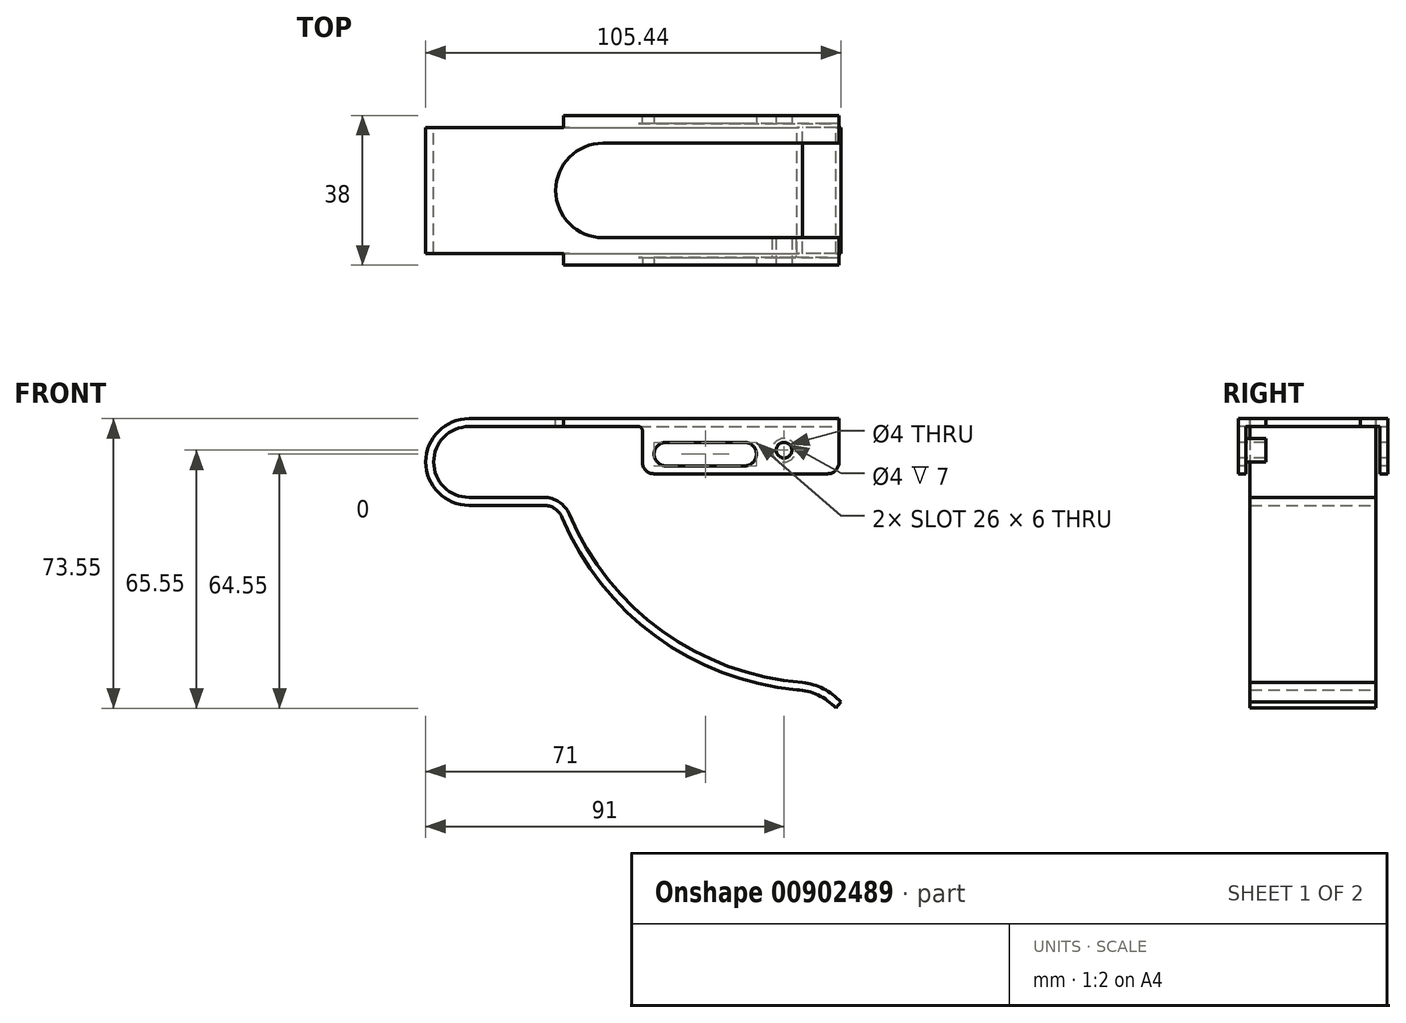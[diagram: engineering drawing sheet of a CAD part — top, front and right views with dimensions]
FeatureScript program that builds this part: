
annotation { "Feature Type Name" : "Feature", "Feature Type Description" : "" }
export const myFeature = defineFeature(function(context is Context, id is Id, definition is map)
    precondition{}
    {
        {
            var Q0;
            Q0=qCreatedBy(makeId("Front.planeOp"),FACE);
            var sketch = newSketch(context, id + "F0", { "sketchPlane" : qUnion([Q0])});
            skArc(sketch, "E0", {"start": v(0, 11) * mm, "mid": v(-11, 0) * mm, "end": v(0, -11) * mm});
            skLineSegment(sketch, "E1", {"start": v(0, 11) * mm, "end": v(94, 11) * mm});
            skLineSegment(sketch, "E2", {"start": v(0, -11) * mm, "end": v(19, -11) * mm});
            skArc(sketch, "E3", {"start": v(23.61, -14.06) * mm, "mid": v(47.38, -44.23) * mm, "end": v(83.28, -57.89) * mm});
            skArc(sketch, "E4", {"start": v(93.14, -62.55) * mm, "mid": v(88.68, -59.22) * mm, "end": v(83.28, -57.89) * mm});
            skPoint(sketch, "E5.visualSharp", {"position": v(22.4, -11) * mm});
            skArc(sketch, "E5.filletArc", {"start": v(23.61, -14.06) * mm, "mid": v(21.77, -11.84) * mm, "end": v(19, -11) * mm});
            skLineSegment(sketch, "E6.0", {"start": v(0, 9) * mm, "end": v(94, 9) * mm});
            skArc(sketch, "E7.0", {"start": v(0, 9) * mm, "mid": v(-9, 0) * mm, "end": v(0, -9) * mm});
            skLineSegment(sketch, "E8.0", {"start": v(0, -9) * mm, "end": v(19, -9) * mm});
            skArc(sketch, "E9.0", {"start": v(25.9, -14.87) * mm, "mid": v(23.53, -10.67) * mm, "end": v(19, -9) * mm});
            skArc(sketch, "E10.0", {"start": v(25.45, -13.3) * mm, "mid": v(49.07, -42.99) * mm, "end": v(84.7, -56) * mm});
            skArc(sketch, "E11.0", {"start": v(94.44, -61) * mm, "mid": v(90.01, -57.64) * mm, "end": v(84.7, -56) * mm});
            skLineSegment(sketch, "E12", {"start": v(93.14, -62.55) * mm, "end": v(94.44, -61) * mm});
            skLineSegment(sketch, "E13", {"start": v(94, 11) * mm, "end": v(94, 9) * mm});
            skLineSegment(sketch, "E14", {"start": v(94.44, -61) * mm, "end": v(131.24, -61) * mm, "construction": true});
            skSolve(sketch);
        }
        {
            var Q0;
            Q0 = qSketchRegion(id + "F0", true);
            extrude(context, id + "F1", {"entities" : qUnion([Q0]), "depth" : 16 * mm, "offsetDistance" : 25 * mm});
        }
        {
            var Q0;
            Q0=makeQuery(id+"F1.opExtrude","SWEPT_FACE",FACE,{"disambiguationData":[OSD([sQuery(id+"F0.wireOp",EDGE,"E1")])]});
            var sketch = newSketch(context, id + "F2", { "sketchPlane" : qUnion([Q0])});
            skLineSegment(sketch, "E15.bottom", {"start": v(94, -16) * mm, "end": v(24, -16) * mm});
            skLineSegment(sketch, "E15.top", {"start": v(94, -19) * mm, "end": v(24, -19) * mm});
            skLineSegment(sketch, "E15.left", {"start": v(94, -16) * mm, "end": v(94, -19) * mm});
            skLineSegment(sketch, "E15.right", {"start": v(24, -16) * mm, "end": v(24, -19) * mm});
            skSolve(sketch);
        }
        {
            var Q0;
            Q0=makeQuery(id+"F2.imprint","IMPRINT",FACE,{"disambiguationData":[TD([[makeQuery(id+"F2.imprint","IMPRINT",EDGE,{"derivedFrom":sQuery(id+"F2.wireOp",EDGE,"E15.bottom")}),-1.0]])]});
            extrude(context, id + "F3", {"entities" : qUnion([Q0]), "operationType" : NewBodyOperationType.ADD, "oppositeDirection" : true, "depth" : 2 * mm, "offsetDistance" : 25 * mm});
        }
        {
            var Q0;
            Q0=makeQuery(id+"F3.opExtrude","SWEPT_FACE",FACE,{"disambiguationData":[OSD([sQuery(id+"F2.wireOp",EDGE,"E15.top")])]});
            var sketch = newSketch(context, id + "F4", { "sketchPlane" : qUnion([Q0])});
            skLineSegment(sketch, "E16.bottom", {"start": v(94, 11) * mm, "end": v(44, 11) * mm});
            skLineSegment(sketch, "E16.top", {"start": v(94, -3) * mm, "end": v(44, -3) * mm});
            skLineSegment(sketch, "E16.left", {"start": v(94, 11) * mm, "end": v(94, -3) * mm});
            skLineSegment(sketch, "E16.right", {"start": v(44, 11) * mm, "end": v(44, -3) * mm});
            skSolve(sketch);
        }
        {
            var Q0;
            Q0 = qSketchRegion(id + "F4", true);
            extrude(context, id + "F5", {"entities" : qUnion([Q0]), "operationType" : NewBodyOperationType.ADD, "oppositeDirection" : true, "depth" : 2 * mm, "offsetDistance" : 25 * mm});
        }
        {
            var Q0;
            Q0=makeQuery(id+"F5.boolean.opBoolean","INTERSECT",EDGE,{"derivedFrom":[makeQuery(id+"F3.boolean.opBoolean","MERGE",FACE,{"derivedFrom":[makeQuery(id+"F1.opExtrude","SWEPT_FACE",FACE,{"disambiguationData":[OSD([sQuery(id+"F0.wireOp",EDGE,"E6.0")])]}),makeQuery(id+"F3.opExtrude","CAP_FACE",FACE,{"disambiguationData":[OSD([sQuery(id+"F2.wireOp",EDGE,"E15.bottom"),sQuery(id+"F2.wireOp",EDGE,"E15.top"),sQuery(id+"F2.wireOp",EDGE,"E15.left"),sQuery(id+"F2.wireOp",EDGE,"E15.right")])],"isStart":false})]}),makeQuery(id+"F5.opExtrude","SWEPT_FACE",FACE,{"disambiguationData":[OSD([sQuery(id+"F4.wireOp",EDGE,"E16.right")])]})]});
            fillet(context, id + "F6", {"entities" : qUnion([Q0]), "radius" : 1 * mm, "tangentPropagation" : true, "allowEdgeOverflow" : false});
        }
        {
            var Q0;
            Q0=makeQuery(id+"F1.opExtrude","SWEPT_BODY",BODY,{"disambiguationData":[OSD([sQuery(id+"F0.wireOp",EDGE,"E0"),sQuery(id+"F0.wireOp",EDGE,"E1"),sQuery(id+"F0.wireOp",EDGE,"E2"),sQuery(id+"F0.wireOp",EDGE,"E3"),sQuery(id+"F0.wireOp",EDGE,"E4"),sQuery(id+"F0.wireOp",EDGE,"E5.filletArc"),sQuery(id+"F0.wireOp",EDGE,"E6.0"),sQuery(id+"F0.wireOp",EDGE,"E7.0"),sQuery(id+"F0.wireOp",EDGE,"E8.0"),sQuery(id+"F0.wireOp",EDGE,"E9.0"),sQuery(id+"F0.wireOp",EDGE,"E10.0"),sQuery(id+"F0.wireOp",EDGE,"E11.0"),sQuery(id+"F0.wireOp",EDGE,"E12"),sQuery(id+"F0.wireOp",EDGE,"E13")])]});
            var Q1;
            Q1=qCreatedBy(makeId("Front.planeOp"),FACE);
            mirror(context, id + "F7", {"operationType" : NewBodyOperationType.ADD, "entities" : qUnion([Q0]), "mirrorPlane" : qUnion([Q1])});
        }
        {
            var Q0;
            {var subQ0=makeQuery(id+"F3.boolean.opBoolean","MERGE",FACE,{"derivedFrom":[makeQuery(id+"F1.opExtrude","SWEPT_FACE",FACE,{"disambiguationData":[OSD([sQuery(id+"F0.wireOp",EDGE,"E1")])]}),makeQuery(id+"F3.opExtrude","CAP_FACE",FACE,{"disambiguationData":[OSD([sQuery(id+"F2.wireOp",EDGE,"E15.bottom"),sQuery(id+"F2.wireOp",EDGE,"E15.top"),sQuery(id+"F2.wireOp",EDGE,"E15.left"),sQuery(id+"F2.wireOp",EDGE,"E15.right")])],"isStart":true})]});Q0=makeQuery(id+"F7.boolean.opBoolean","MERGE",FACE,{"derivedFrom":[subQ0,makeQuery(id+"F7.opPattern","COPY",FACE,{"derivedFrom":subQ0,"instanceName":"1"})]});}
            var sketch = newSketch(context, id + "F8", { "sketchPlane" : qUnion([Q0])});
            skArc(sketch, "E17", {"start": v(34, 12) * mm, "mid": v(22, 0) * mm, "end": v(34, -12) * mm});
            skLineSegment(sketch, "E18", {"start": v(34, 12) * mm, "end": v(94, 12) * mm});
            skLineSegment(sketch, "E19", {"start": v(34, -12) * mm, "end": v(94, -12) * mm});
            skLineSegment(sketch, "E20", {"start": v(94, 12) * mm, "end": v(94, -12) * mm});
            skSolve(sketch);
        }
        {
            var Q0;
            Q0 = qSketchRegion(id + "F8", true);
            extrude(context, id + "F9", {"entities" : qUnion([Q0]), "operationType" : NewBodyOperationType.REMOVE, "oppositeDirection" : true, "depth" : 2 * mm, "offsetDistance" : 25 * mm});
        }
        {
            var Q0;
            Q0=makeQuery(id+"F5.boolean.opBoolean","MERGE",FACE,{"derivedFrom":[makeQuery(id+"F3.opExtrude","SWEPT_FACE",FACE,{"disambiguationData":[OSD([sQuery(id+"F2.wireOp",EDGE,"E15.top")])]}),makeQuery(id+"F5.opExtrude","CAP_FACE",FACE,{"disambiguationData":[OSD([sQuery(id+"F4.wireOp",EDGE,"E16.bottom"),sQuery(id+"F4.wireOp",EDGE,"E16.top"),sQuery(id+"F4.wireOp",EDGE,"E16.left"),sQuery(id+"F4.wireOp",EDGE,"E16.right")])],"isStart":true})]});
            var sketch = newSketch(context, id + "F10", { "sketchPlane" : qUnion([Q0])});
            skLineSegment(sketch, "E21", {"start": v(50, 2) * mm, "end": v(70, 2) * mm});
            skArc(sketch, "E22.0.startCap", {"start": v(50, -1) * mm, "mid": v(47, 2) * mm, "end": v(50, 5) * mm});
            skArc(sketch, "E22.0.endCap", {"start": v(70, 5) * mm, "mid": v(73, 2) * mm, "end": v(70, -1) * mm});
            skLineSegment(sketch, "E22.0.left", {"start": v(50, 5) * mm, "end": v(70, 5) * mm});
            skLineSegment(sketch, "E22.0.right", {"start": v(50, -1) * mm, "end": v(70, -1) * mm});
            skSolve(sketch);
        }
        {
            var Q0;
            Q0 = qSketchRegion(id + "F10", true);
            extrude(context, id + "F11", {"entities" : qUnion([Q0]), "operationType" : NewBodyOperationType.REMOVE, "endBound" : BoundingType.THROUGH_ALL, "oppositeDirection" : true, "depth" : 25 * mm, "offsetDistance" : 25 * mm});
        }
        {
            var Q0;
            Q0=makeQuery(id+"F5.boolean.opBoolean","MERGE",FACE,{"derivedFrom":[makeQuery(id+"F3.opExtrude","SWEPT_FACE",FACE,{"disambiguationData":[OSD([sQuery(id+"F2.wireOp",EDGE,"E15.top")])]}),makeQuery(id+"F5.opExtrude","CAP_FACE",FACE,{"disambiguationData":[OSD([sQuery(id+"F4.wireOp",EDGE,"E16.bottom"),sQuery(id+"F4.wireOp",EDGE,"E16.top"),sQuery(id+"F4.wireOp",EDGE,"E16.left"),sQuery(id+"F4.wireOp",EDGE,"E16.right")])],"isStart":true})]});
            var sketch = newSketch(context, id + "F12", { "sketchPlane" : qUnion([Q0])});
            skPoint(sketch, "E23", {"position": v(80, 3) * mm});
            skSolve(sketch);
        }
        {
            var Q0;
            Q0=sQuery(id+"F12.wireOp",VERTEX,"E23");
            var Q1;
            Q1=makeQuery(id+"F1.opExtrude","SWEPT_BODY",BODY,{"disambiguationData":[OSD([sQuery(id+"F0.wireOp",EDGE,"E0"),sQuery(id+"F0.wireOp",EDGE,"E1"),sQuery(id+"F0.wireOp",EDGE,"E2"),sQuery(id+"F0.wireOp",EDGE,"E3"),sQuery(id+"F0.wireOp",EDGE,"E4"),sQuery(id+"F0.wireOp",EDGE,"E5.filletArc"),sQuery(id+"F0.wireOp",EDGE,"E6.0"),sQuery(id+"F0.wireOp",EDGE,"E7.0"),sQuery(id+"F0.wireOp",EDGE,"E8.0"),sQuery(id+"F0.wireOp",EDGE,"E9.0"),sQuery(id+"F0.wireOp",EDGE,"E10.0"),sQuery(id+"F0.wireOp",EDGE,"E11.0"),sQuery(id+"F0.wireOp",EDGE,"E12"),sQuery(id+"F0.wireOp",EDGE,"E13")])]});
            hole(context, id + "F13", {"style" : HoleStyle.SIMPLE, "endStyle" : HoleEndStyle.THROUGH, "holeDiameter" : 4 * mm, "majorDiameter" : 5 * mm, "isTappedThrough" : true, "tappedDepth" : 12 * mm, "tapClearance" : 3, "locations" : qUnion([Q0]), "scope" : qUnion([Q1])});
        }
        {
            var Q0;
            Q0=makeQuery(id+"F5.opExtrude","CAP_FACE",FACE,{"disambiguationData":[OSD([sQuery(id+"F4.wireOp",EDGE,"E16.bottom"),sQuery(id+"F4.wireOp",EDGE,"E16.top"),sQuery(id+"F4.wireOp",EDGE,"E16.left"),sQuery(id+"F4.wireOp",EDGE,"E16.right")])],"isStart":false});
            var sketch = newSketch(context, id + "F14", { "sketchPlane" : qUnion([Q0])});
            skCircle(sketch, "E24.0", {"center": v(-80, 3) * mm, "radius": 2 * mm});
            skCircle(sketch, "E25.0", {"center": v(-80, 3) * mm, "radius": 3 * mm});
            skSolve(sketch);
        }
        {
            var Q0;
            Q0 = qSketchRegion(id + "F14", true);
            extrude(context, id + "F15", {"entities" : qUnion([Q0]), "operationType" : NewBodyOperationType.ADD, "depth" : 5 * mm, "offsetDistance" : 25 * mm});
        }
        {
            var Q0;
            Q0=makeQuery(id+"F5.opExtrude","SWEPT_EDGE",EDGE,{"disambiguationData":[OSD([sQuery(id+"F4.wireOp",EDGE,"E16.top"),sQuery(id+"F4.wireOp",EDGE,"E16.left")])]});
            var Q1;
            Q1=makeQuery(id+"F5.opExtrude","SWEPT_EDGE",EDGE,{"disambiguationData":[OSD([sQuery(id+"F4.wireOp",EDGE,"E16.top"),sQuery(id+"F4.wireOp",EDGE,"E16.right")])]});
            var Q2;
            Q2=makeQuery(id+"F7.opPattern","COPY",EDGE,{"derivedFrom":makeQuery(id+"F5.opExtrude","SWEPT_EDGE",EDGE,{"disambiguationData":[OSD([sQuery(id+"F4.wireOp",EDGE,"E16.top"),sQuery(id+"F4.wireOp",EDGE,"E16.left")])]}),"instanceName":"1"});
            var Q3;
            Q3=makeQuery(id+"F7.opPattern","COPY",EDGE,{"derivedFrom":makeQuery(id+"F5.opExtrude","SWEPT_EDGE",EDGE,{"disambiguationData":[OSD([sQuery(id+"F4.wireOp",EDGE,"E16.top"),sQuery(id+"F4.wireOp",EDGE,"E16.right")])]}),"instanceName":"1"});
            fillet(context, id + "F16", {"entities" : qUnion([Q0, Q1, Q2, Q3]), "radius" : 3 * mm, "tangentPropagation" : true, "allowEdgeOverflow" : false});
        }
    });
